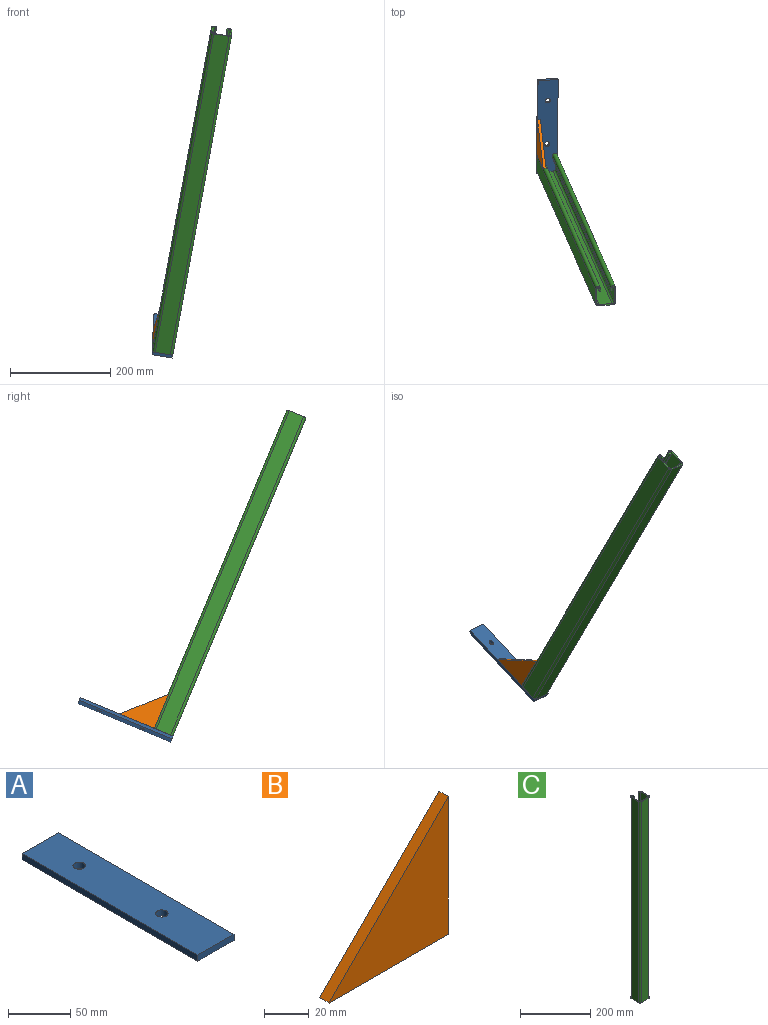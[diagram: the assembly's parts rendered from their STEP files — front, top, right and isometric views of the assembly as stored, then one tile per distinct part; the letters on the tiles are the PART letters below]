
ASSEMBLY  parts=3 mates=2
PART A: 8 faces, bbox 41x200x6 mm
  f0: plane 41x6mm, normal (0,1,0), area 246mm2, adj f1,f4,f6,f7
  f1: plane 200x6mm, normal (-1,0,0), area 1200mm2, adj f0,f2,f6,f7
  f2: plane 41x6mm, normal (0,-1,0), area 246mm2, adj f1,f4,f6,f7
  f3: cylinder r=5mm len=10mm, axis (0,0,-1), area 188.5mm2, adj f6,f7
  f4: plane 200x6mm, normal (1,0,0), area 1200mm2, adj f0,f2,f6,f7
  f5: cylinder r=5mm len=10mm, axis (0,0,-1), area 188.5mm2, adj f6,f7
  f6: plane 200x41mm, normal (0,0,1), area 8042.9mm2, adj f0,f1,f2,f3,f4,f5
  f7: plane 200x41mm, normal (0,0,-1), area 8042.9mm2, adj f0,f1,f2,f3,f4,f5
PART B: 5 faces, bbox 75x6x75 mm
  f0: plane 75x6mm, normal (0,0,-1), area 450mm2, adj f1,f2,f3,f4
  f1: plane 75x6mm, normal (1,0,0), area 450mm2, adj f0,f2,f3,f4
  f2: plane 75x75mm, normal (-0.71,0,0.71), area 636.4mm2, adj f0,f1,f3,f4
  f3: plane 75x75mm, normal (0,-1,0), area 2812.5mm2, adj f0,f1,f2
  f4: plane 75x75mm, normal (0,1,0), area 2812.5mm2, adj f0,f1,f2
PART C: 22 faces, bbox 41x41x700 mm
  f0: plane 700x31mm, normal (-1,0,0), area 21700mm2, adj f1,f19,f20,f21
  f1: cylinder r=5mm len=700mm, axis (0,0,-1), area 5497.8mm2, adj f0,f2,f20,f21
  f2: plane 700x31mm, normal (0,-1,0), area 21700mm2, adj f1,f3,f20,f21
  f3: cylinder r=5mm len=700mm, axis (0,0,-1), area 5497.8mm2, adj f2,f4,f20,f21
  f4: plane 700x31mm, normal (1,0,0), area 21700mm2, adj f3,f5,f20,f21
  f5: cylinder r=5mm len=700mm, axis (0,0,-1), area 10995.6mm2, adj f4,f6,f20,f21
  f6: plane 700x5mm, normal (-1,0,0), area 3500mm2, adj f5,f7,f20,f21
  f7: plane 700x2.5mm, normal (0,-1,0), area 1750mm2, adj f6,f8,f20,f21
  f8: plane 700x5mm, normal (1,0,0), area 3500mm2, adj f7,f9,f20,f21
  f9: cylinder r=2.5mm len=700mm, axis (0,0,-1), area 5497.8mm2, adj f8,f10,f20,f21
  f10: plane 700x28.5mm, normal (-1,0,0), area 19950mm2, adj f9,f11,f20,f21
  f11: cylinder r=5mm len=700mm, axis (0,0,-1), area 5497.8mm2, adj f10,f12,f20,f21
  f12: plane 700x26mm, normal (0,1,0), area 18200mm2, adj f11,f13,f20,f21
  f13: cylinder r=5mm len=700mm, axis (0,0,-1), area 5497.8mm2, adj f12,f14,f20,f21
  f14: plane 700x28.5mm, normal (1,0,0), area 19950mm2, adj f13,f15,f20,f21
  f15: cylinder r=2.5mm len=700mm, axis (0,0,-1), area 5497.8mm2, adj f14,f16,f20,f21
  f16: plane 700x5mm, normal (-1,0,0), area 3500mm2, adj f15,f17,f20,f21
  f17: plane 700x2.5mm, normal (0,-1,0), area 1750mm2, adj f16,f18,f20,f21
  f18: plane 700x5mm, normal (1,0,0), area 3500mm2, adj f17,f19,f20,f21
  f19: cylinder r=5mm len=700mm, axis (0,0,-1), area 10995.6mm2, adj f0,f18,f20,f21
  f20: plane 41x41mm, normal (0,0,1), area 353.9mm2, adj f0,f1,f2,f3,f4,f5,f6,f7
  f21: plane 41x41mm, normal (0,0,-1), area 353.9mm2, adj f0,f1,f2,f3,f4,f5,f6,f7
PLACE A rot(axis=(0.92,0.39,0.04),24.6deg) t=(-28.9,150.63,-418.23)mm
PLACE B rot(axis=(0.11,0.28,-0.95),91.5deg) t=(-73.31,173.47,-393.89)mm
PLACE C rot(axis=(0.92,0.39,0.04),24.6deg) t=(-58.06,158.61,-402.92)mm
MATE fastened B.f3 <-> A.f1  axis (-0.99,-0.05,0.16) through (-79.23,173.17,-392.92)mm
MATE fastened A.f6 <-> C.f21  axis (0.17,-0.38,0.91) through (-59.59,137.29,-411.56)mm
